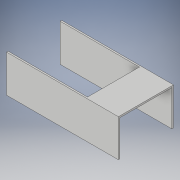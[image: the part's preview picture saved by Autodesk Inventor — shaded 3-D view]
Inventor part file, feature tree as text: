
AUTODESK INVENTOR PART (.ipt)
format: ipt  version: 2017 (Build 210142000, 142)  size: 132,608 bytes
history: native  units: in
note: dims shown in document units (in); Inventor stores cm internally (conversion verified against a paired STEP export)
features: extrude x6, sketch x6
ambient origin geometry x8: Origin, YZ Plane, XZ Plane, XY Plane, X Axis, Y Axis, Z Axis, Center Point
bodies: Solid1 (feature_tree)
feature tree (12):
  extrude  "Extrusion1"  Depth=5.75in
  extrude  "Extrusion2"  Depth=5.0in
  extrude  "Extrusion3"  Depth=8.0in TaperAngle=0.0deg
  extrude  "Extrusion4"  Depth=5.5in TaperAngle=0.0deg
  extrude  "Extrusion5"  Depth=13.5in TaperAngle=0.0deg
  extrude  "Extrusion6"  [1 undecoded]
  sketch  "Sketch1"  dims[d0=3.75in d1=5.75in]
  sketch  "Sketch2"  dims[d2=0.25in d3=0.0in d4=5.0in]
  sketch  "Sketch3"  dims[d5=0.25in d6=8.0in d7=0.0in]
  sketch  "Sketch4"  dims[d8=0.25in d9=0.0in d10=5.5in d11=0.0in]
  sketch  "Sketch5"  dims[d12=13.5in d13=0.0in d14=13.5in d15=0.0in]
  sketch  "Sketch6"
note: 1 required parameter value undecoded (feature->parameter linkage not recoverable at this tier; creation-order binding heuristic only, values carry confidence <= 0.55)
